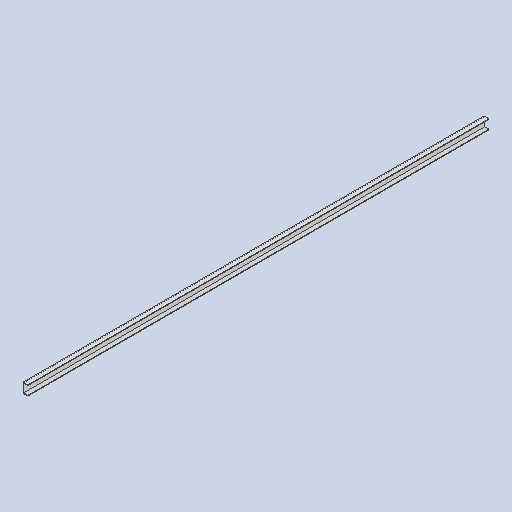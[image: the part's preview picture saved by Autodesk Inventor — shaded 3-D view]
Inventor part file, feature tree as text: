
AUTODESK INVENTOR PART (.ipt)
format: ipt  version: 2023 (Build 270158030, 158C)  size: 90,112 bytes
history: native  units: in
note: dims shown in document units (in); Inventor stores cm internally (conversion verified against a paired STEP export)
features: extrude x1, sketch x1
ambient origin geometry x8: Origin, YZ Plane, XZ Plane, XY Plane, X Axis, Y Axis, Z Axis, Center Point
bodies: Solid1 (feature_tree)
feature tree (2):
  extrude  "Extrusion1"  Depth=0.125in
  sketch  "Sketch1"  dims[d0=1.0in d1=0.125in d2=0.875in d3=1.75in d4=0.875in d5=0.125in d6=96.0in d7=0.0in]
